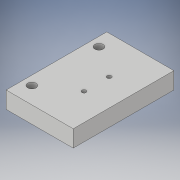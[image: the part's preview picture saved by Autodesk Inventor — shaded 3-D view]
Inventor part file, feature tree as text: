
AUTODESK INVENTOR PART (.ipt)
format: ipt  version: 2017 (Build 210142000, 142)  size: 103,936 bytes
history: native  units: in
note: dims shown in document units (in); Inventor stores cm internally (conversion verified against a paired STEP export)
features: extrude x1, sketch x1
ambient origin geometry x8: Origin, YZ Plane, XZ Plane, XY Plane, X Axis, Y Axis, Z Axis, Center Point
bodies: Solid1 (feature_tree)
feature tree (2):
  extrude  "Extrusion1"  Depth=1.5in
  sketch  "Sketch1"  dims[d0=1.0in d1=1.5in d2=0.678in d3=0.188in d4=0.5in d5=0.125in d6=0.276in d7=0.1875in d8=0.063in d9=0.25in d10=0.0in]
